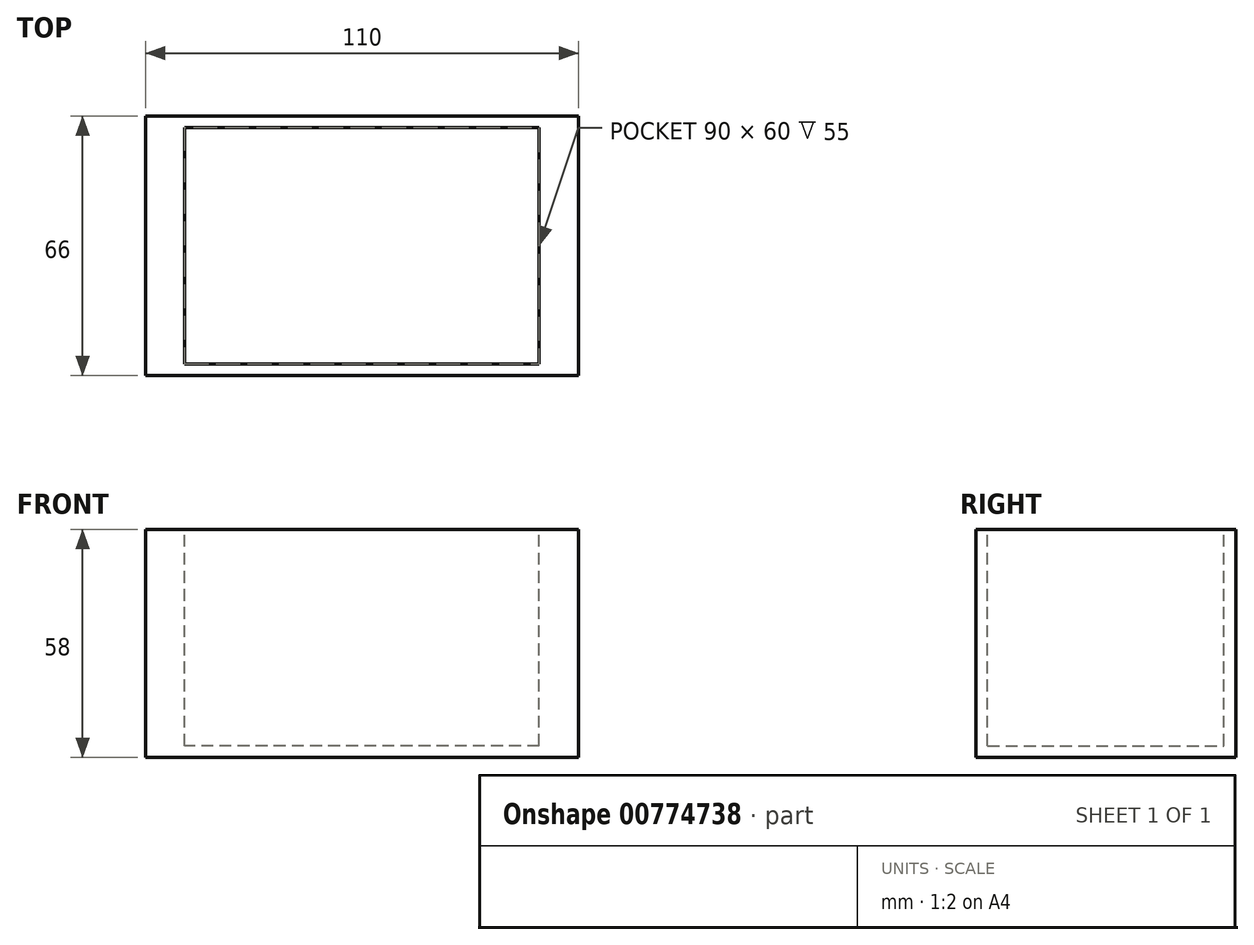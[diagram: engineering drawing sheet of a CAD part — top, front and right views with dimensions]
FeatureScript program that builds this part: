
annotation { "Feature Type Name" : "Feature", "Feature Type Description" : "" }
export const myFeature = defineFeature(function(context is Context, id is Id, definition is map)
    precondition{}
    {
        {
            var Q0;
            Q0=qCreatedBy(makeId("Top.planeOp"),FACE);
            var sketch = newSketch(context, id + "F0", { "sketchPlane" : qUnion([Q0])});
            skLineSegment(sketch, "E0.bottom", {"start": v(-45, 30) * mm, "end": v(45, 30) * mm});
            skLineSegment(sketch, "E0.top", {"start": v(-45, -30) * mm, "end": v(45, -30) * mm});
            skLineSegment(sketch, "E0.left", {"start": v(-45, 30) * mm, "end": v(-45, -30) * mm});
            skLineSegment(sketch, "E0.right", {"start": v(45, 30) * mm, "end": v(45, -30) * mm});
            skPoint(sketch, "E0.middle", {"position": v(0, 0) * mm});
            skLineSegment(sketch, "E1.0", {"start": v(-48, 33) * mm, "end": v(48, 33) * mm});
            skLineSegment(sketch, "E1.2", {"start": v(-48, -33) * mm, "end": v(48, -33) * mm});
            skLineSegment(sketch, "E2.1", {"start": v(-55, 33) * mm, "end": v(-55, -33) * mm});
            skLineSegment(sketch, "E2.3", {"start": v(55, 33) * mm, "end": v(55, -33) * mm});
            skLineSegment(sketch, "E3", {"start": v(-48, 33) * mm, "end": v(-55, 33) * mm});
            skLineSegment(sketch, "E4", {"start": v(-55, 33) * mm, "end": v(-48, 33) * mm});
            skLineSegment(sketch, "E5", {"start": v(-48, -33) * mm, "end": v(-55, -33) * mm});
            skLineSegment(sketch, "E6", {"start": v(48, 33) * mm, "end": v(55, 33) * mm});
            skLineSegment(sketch, "E7", {"start": v(48, -33) * mm, "end": v(55, -33) * mm});
            skPoint(sketch, "E8.end.orphan", {"position": v(48, 40) * mm});
            skPoint(sketch, "E9.orphan", {"position": v(-55, 40) * mm});
            skPoint(sketch, "E10.end.orphan", {"position": v(-48, 40) * mm});
            skPoint(sketch, "E11.orphan", {"position": v(-55, -40) * mm});
            skPoint(sketch, "E12.end.orphan", {"position": v(-48, -40) * mm});
            skPoint(sketch, "E13.end.orphan", {"position": v(48, -40) * mm});
            skSolve(sketch);
        }
        {
            var Q0;
            Q0=makeQuery(id+"F0.imprint","IMPRINT",FACE,{"disambiguationData":[TD([[makeQuery(id+"F0.imprint","IMPRINT",EDGE,{"derivedFrom":sQuery(id+"F0.wireOp",EDGE,"E0.bottom")}),1.0]])]});
            var Q1;
            Q1=makeQuery(id+"F0.imprint","IMPRINT",FACE,{"disambiguationData":[TD([[makeQuery(id+"F0.imprint","IMPRINT",EDGE,{"derivedFrom":sQuery(id+"F0.wireOp",EDGE,"E0.bottom")}),-1.0]])]});
            extrude(context, id + "F1", {"entities" : qUnion([Q0, Q1]), "depth" : 58 * mm, "offsetDistance" : 25 * mm});
        }
        {
            var Q0;
            Q0=makeQuery(id+"F1.opExtrude","CAP_FACE",FACE,{"disambiguationData":[OSD([sQuery(id+"F0.wireOp",EDGE,"E1.0"),sQuery(id+"F0.wireOp",EDGE,"E1.2"),sQuery(id+"F0.wireOp",EDGE,"E2.1"),sQuery(id+"F0.wireOp",EDGE,"E2.3"),sQuery(id+"F0.wireOp",EDGE,"E4"),sQuery(id+"F0.wireOp",EDGE,"E5"),sQuery(id+"F0.wireOp",EDGE,"E6"),sQuery(id+"F0.wireOp",EDGE,"E7")])],"isStart":false});
            var sketch = newSketch(context, id + "F2", { "sketchPlane" : qUnion([Q0])});
            skLineSegment(sketch, "E14.bottom", {"start": v(45, -30) * mm, "end": v(-45, -30) * mm});
            skLineSegment(sketch, "E14.top", {"start": v(45, 30) * mm, "end": v(-45, 30) * mm});
            skLineSegment(sketch, "E14.left", {"start": v(45, -30) * mm, "end": v(45, 30) * mm});
            skLineSegment(sketch, "E14.right", {"start": v(-45, -30) * mm, "end": v(-45, 30) * mm});
            skPoint(sketch, "E14.middle", {"position": v(0, 0) * mm});
            skSolve(sketch);
        }
        {
            var Q0;
            Q0=makeQuery(id+"F2.imprint","IMPRINT",FACE,{"disambiguationData":[TD([[makeQuery(id+"F2.imprint","IMPRINT",EDGE,{"derivedFrom":sQuery(id+"F2.wireOp",EDGE,"E14.bottom")}),-1.0]])]});
            extrude(context, id + "F3", {"entities" : qUnion([Q0]), "operationType" : NewBodyOperationType.REMOVE, "oppositeDirection" : true, "depth" : 55 * mm, "offsetDistance" : 25 * mm});
        }
    });
